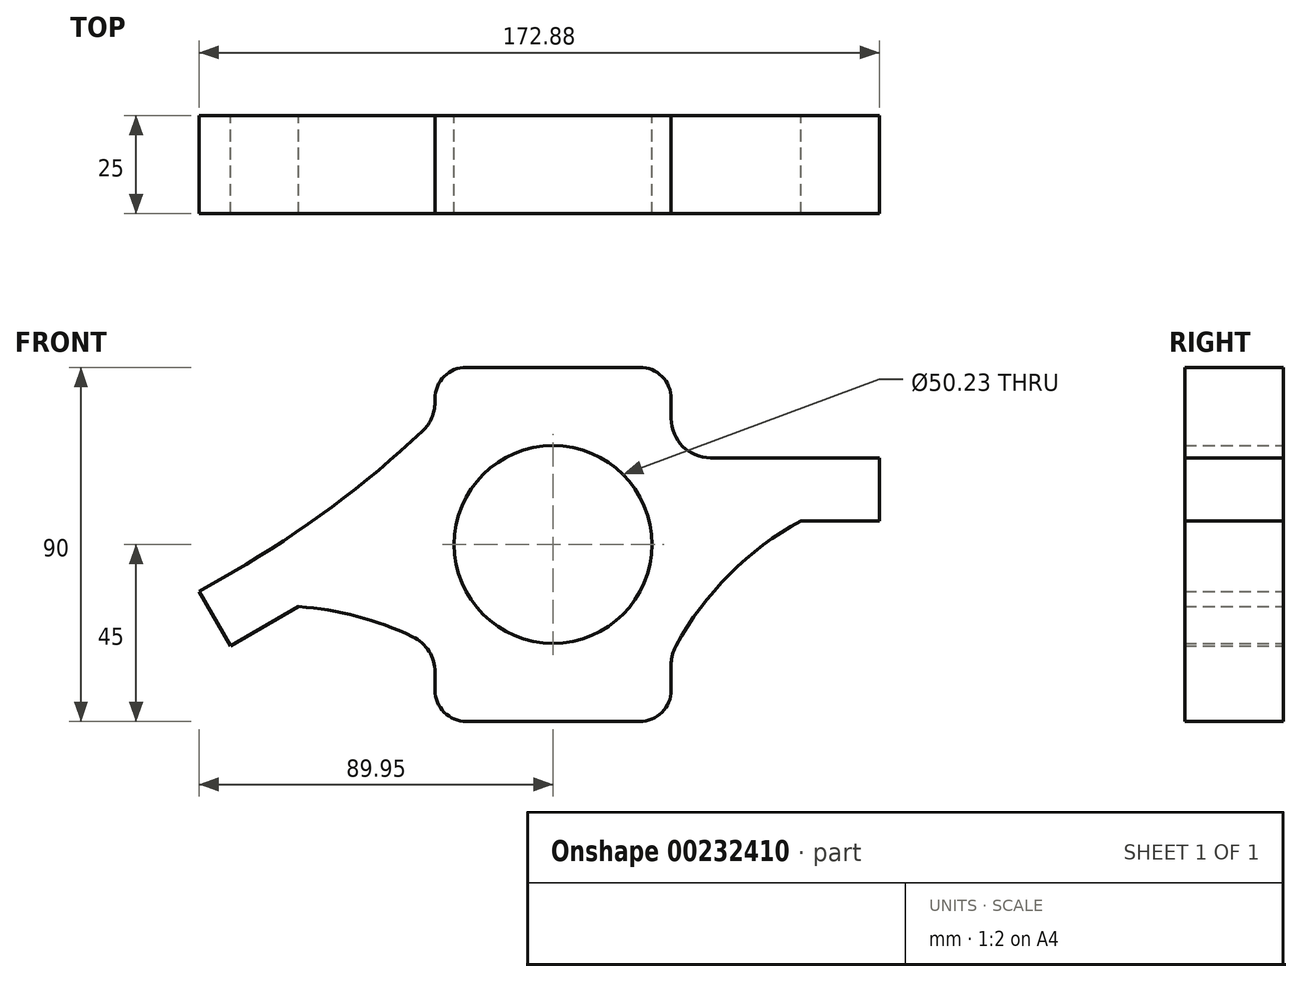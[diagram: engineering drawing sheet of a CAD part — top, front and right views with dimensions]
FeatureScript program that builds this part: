
annotation { "Feature Type Name" : "Feature", "Feature Type Description" : "" }
export const myFeature = defineFeature(function(context is Context, id is Id, definition is map)
    precondition{}
    {
        {
            var Q0;
            Q0=qCreatedBy(makeId("Front.planeOp"),FACE);
            var sketch = newSketch(context, id + "F0", { "sketchPlane" : qUnion([Q0])});
            skCircle(sketch, "E0", {"center": v(0, 0) * mm, "radius": 25.11 * mm});
            skCircle(sketch, "E1", {"center": v(0, 0) * mm, "radius": 40 * mm, "construction": true});
            skLineSegment(sketch, "E2", {"start": v(0, 29) * mm, "end": v(-72.62, -12.92) * mm, "construction": true});
            skLineSegment(sketch, "E3", {"start": v(-22, 45) * mm, "end": v(22, 45) * mm});
            skLineSegment(sketch, "E4", {"start": v(30, 37) * mm, "end": v(30, 32) * mm});
            skLineSegment(sketch, "E5", {"start": v(-30, 37) * mm, "end": v(-30, 36.1) * mm});
            skLineSegment(sketch, "E6", {"start": v(-30, -32.47) * mm, "end": v(-30, -37) * mm});
            skLineSegment(sketch, "E7", {"start": v(-22, -45) * mm, "end": v(22, -45) * mm});
            skLineSegment(sketch, "E8", {"start": v(30, -37) * mm, "end": v(30, -30.56) * mm});
            skLineSegment(sketch, "E9", {"start": v(40, 22) * mm, "end": v(82.93, 22) * mm});
            skLineSegment(sketch, "E10", {"start": v(82.93, 22) * mm, "end": v(82.93, 6) * mm});
            skLineSegment(sketch, "E11", {"start": v(82.93, 6) * mm, "end": v(62.93, 6) * mm});
            skArc(sketch, "E12", {"start": v(62.93, 6) * mm, "mid": v(44.8, -7.61) * mm, "end": v(31.22, -25.77) * mm});
            skPoint(sketch, "E13.orphan", {"position": v(30, 1.35) * mm});
            skPoint(sketch, "E14.orphan", {"position": v(30, -21.82) * mm});
            skPoint(sketch, "E15.visualSharp", {"position": v(30, -28.1) * mm});
            skArc(sketch, "E15.filletArc", {"start": v(31.22, -25.77) * mm, "mid": v(30.31, -28.09) * mm, "end": v(30, -30.56) * mm});
            skPoint(sketch, "E16.visualSharp", {"position": v(30, 22) * mm});
            skArc(sketch, "E16.filletArc", {"start": v(30, 32) * mm, "mid": v(32.93, 24.93) * mm, "end": v(40, 22) * mm});
            skPoint(sketch, "E17.visualSharp", {"position": v(30, 45) * mm});
            skArc(sketch, "E17.filletArc", {"start": v(30, 37) * mm, "mid": v(27.66, 42.66) * mm, "end": v(22, 45) * mm});
            skPoint(sketch, "E18.visualSharp", {"position": v(-30, 45) * mm});
            skArc(sketch, "E18.filletArc", {"start": v(-22, 45) * mm, "mid": v(-27.66, 42.66) * mm, "end": v(-30, 37) * mm});
            skPoint(sketch, "E19.visualSharp", {"position": v(30, -45) * mm});
            skArc(sketch, "E19.filletArc", {"start": v(22, -45) * mm, "mid": v(27.66, -42.66) * mm, "end": v(30, -37) * mm});
            skLineSegment(sketch, "E20", {"start": v(-81.95, -25.82) * mm, "end": v(-64.63, -15.82) * mm});
            skLineSegment(sketch, "E21", {"start": v(-81.95, -25.82) * mm, "end": v(-89.95, -11.96) * mm});
            skLineSegment(sketch, "E22", {"start": v(-89.95, -11.96) * mm, "end": v(-81.29, -6.96) * mm});
            skArc(sketch, "E23", {"start": v(-35.69, -23.45) * mm, "mid": v(-49.8, -18.27) * mm, "end": v(-64.63, -15.82) * mm});
            skArc(sketch, "E24", {"start": v(-81.29, -6.96) * mm, "mid": v(-56.18, 9.54) * mm, "end": v(-33.15, 28.82) * mm});
            skArc(sketch, "E25", {"start": v(-33.15, 28.82) * mm, "mid": v(-30.82, 32.14) * mm, "end": v(-30, 36.1) * mm});
            skPoint(sketch, "E26.visualSharp", {"position": v(-30, -26.46) * mm});
            skArc(sketch, "E26.filletArc", {"start": v(-30, -32.47) * mm, "mid": v(-31.54, -27.14) * mm, "end": v(-35.69, -23.45) * mm});
            skPoint(sketch, "E27.visualSharp", {"position": v(-30, -45) * mm});
            skArc(sketch, "E27.filletArc", {"start": v(-30, -37) * mm, "mid": v(-27.66, -42.66) * mm, "end": v(-22, -45) * mm});
            skSolve(sketch);
        }
        {
            var Q0;
            Q0=makeQuery(id+"F0.imprint","IMPRINT",FACE,{"disambiguationData":[TD([[makeQuery(id+"F0.imprint","IMPRINT",EDGE,{"derivedFrom":sQuery(id+"F0.wireOp",EDGE,"E0")}),-1.0]])]});
            extrude(context, id + "F1", {"entities" : qUnion([Q0]), "depth" : 25 * mm});
        }
    });
